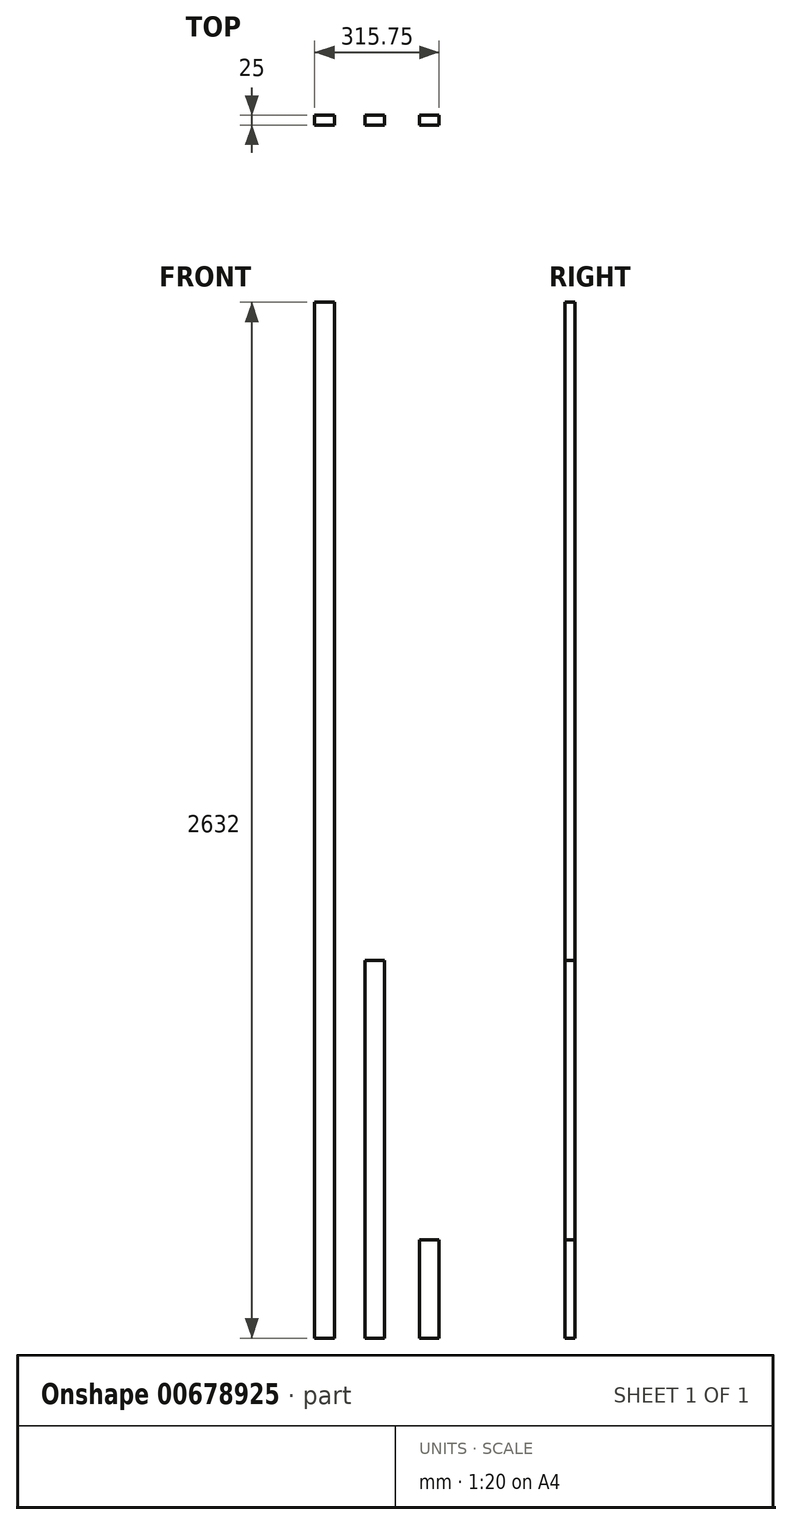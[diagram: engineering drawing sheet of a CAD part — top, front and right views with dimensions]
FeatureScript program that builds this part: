
annotation { "Feature Type Name" : "Feature", "Feature Type Description" : "" }
export const myFeature = defineFeature(function(context is Context, id is Id, definition is map)
    precondition{}
    {
        {
            var Q0;
            Q0=qCreatedBy(makeId("Front.planeOp"),FACE);
            var sketch = newSketch(context, id + "F0", { "sketchPlane" : qUnion([Q0])});
            skLineSegment(sketch, "E0.bottom", {"start": v(0, 0) * mm, "end": v(50, 0) * mm});
            skLineSegment(sketch, "E0.top", {"start": v(0, 2632) * mm, "end": v(50, 2632) * mm});
            skLineSegment(sketch, "E0.left", {"start": v(0, 0) * mm, "end": v(0, 2632) * mm});
            skLineSegment(sketch, "E0.right", {"start": v(50, 0) * mm, "end": v(50, 2632) * mm});
            skSolve(sketch);
        }
        {
            var Q0;
            Q0=makeQuery(id+"F0.imprint","IMPRINT",FACE,{"disambiguationData":[TD([[makeQuery(id+"F0.imprint","IMPRINT",EDGE,{"derivedFrom":sQuery(id+"F0.wireOp",EDGE,"E0.bottom")}),1.0]])]});
            extrude(context, id + "F1", {"entities" : qUnion([Q0]), "depth" : 25 * mm, "offsetDistance" : 25 * mm});
        }
        {
            var Q0;
            Q0=qCreatedBy(makeId("Front.planeOp"),FACE);
            var sketch = newSketch(context, id + "F2", { "sketchPlane" : qUnion([Q0])});
            skLineSegment(sketch, "E1.bottom", {"start": v(127.67, 0) * mm, "end": v(177.67, 0) * mm});
            skLineSegment(sketch, "E1.top", {"start": v(127.67, 960) * mm, "end": v(177.67, 960) * mm});
            skLineSegment(sketch, "E1.left", {"start": v(127.67, 0) * mm, "end": v(127.67, 960) * mm});
            skLineSegment(sketch, "E1.right", {"start": v(177.67, 0) * mm, "end": v(177.67, 960) * mm});
            skSolve(sketch);
        }
        {
            var Q0;
            Q0=qSketchRegion(id+"F2",true);
            extrude(context, id + "F3", {"entities" : qUnion([Q0]), "depth" : 25 * mm, "offsetDistance" : 25 * mm});
        }
        {
            var Q0;
            Q0=qCreatedBy(makeId("Front.planeOp"),FACE);
            var sketch = newSketch(context, id + "F4", { "sketchPlane" : qUnion([Q0])});
            skLineSegment(sketch, "E2.bottom", {"start": v(265.75, 0) * mm, "end": v(315.75, 0) * mm});
            skLineSegment(sketch, "E2.top", {"start": v(265.75, 250) * mm, "end": v(315.75, 250) * mm});
            skLineSegment(sketch, "E2.left", {"start": v(265.75, 0) * mm, "end": v(265.75, 250) * mm});
            skLineSegment(sketch, "E2.right", {"start": v(315.75, 0) * mm, "end": v(315.75, 250) * mm});
            skSolve(sketch);
        }
        {
            var Q0;
            Q0=qSketchRegion(id+"F4",true);
            extrude(context, id + "F5", {"entities" : qUnion([Q0]), "depth" : 25 * mm, "offsetDistance" : 25 * mm});
        }
    });
